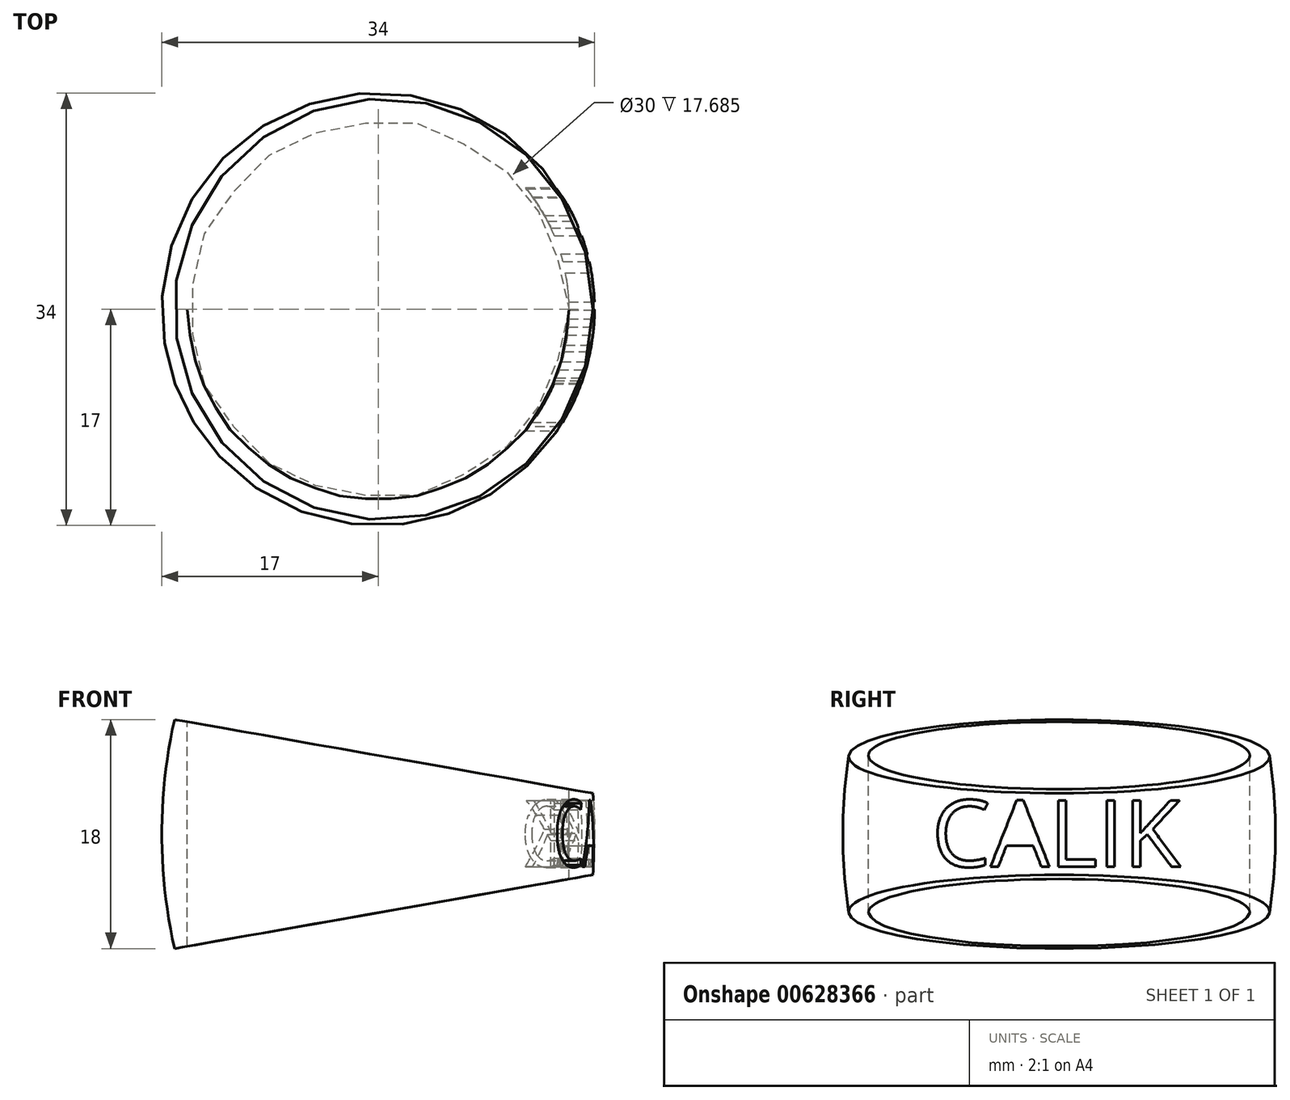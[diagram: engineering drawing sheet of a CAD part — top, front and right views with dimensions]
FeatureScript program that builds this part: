
annotation { "Feature Type Name" : "Feature", "Feature Type Description" : "" }
export const myFeature = defineFeature(function(context is Context, id is Id, definition is map)
    precondition{}
    {
        {
            var Q0;
            Q0=qCreatedBy(makeId("Front.planeOp"),FACE);
            var sketch = newSketch(context, id + "F0", { "sketchPlane" : qUnion([Q0])});
            skPoint(sketch, "E0", {"position": v(17, 0) * mm});
            skArc(sketch, "E1", {"start": v(16, -9) * mm, "mid": v(17, 0) * mm, "end": v(16, 9) * mm});
            skLineSegment(sketch, "E2", {"start": v(16, 9) * mm, "end": v(15, 9) * mm});
            skLineSegment(sketch, "E3", {"start": v(15, 9) * mm, "end": v(15, -9) * mm});
            skLineSegment(sketch, "E4", {"start": v(15, -9) * mm, "end": v(16, -9) * mm});
            skLineSegment(sketch, "E5", {"start": v(0, 0) * mm, "end": v(0, -4.95) * mm, "construction": true});
            skSolve(sketch);
        }
        {
            var Q0;
            Q0 = qSketchRegion(id + "F0", true);
            var Q1;
            Q1 = qConstructionFilter(qBodyType(qCreatedBy(id + "F0" ,EDGE), BodyType.WIRE), ConstructionObject.NO);
            var Q2;
            Q2=sQuery(id+"F0.wireOp",EDGE,"E5");
            revolve(context, id + "F1", {"entities" : qUnion([Q0]), "surfaceEntities" : qUnion([Q1]), "axis" : qUnion([Q2]), "revolveType" : RevolveType.FULL});
        }
        {
            var Q0;
            Q0=qCreatedBy(makeId("Front.planeOp"),FACE);
            cPlane(context, id + "F2", {"entities" : qUnion([Q0]), "cplaneType" : CPlaneType.OFFSET, "offset" : (17) * mm, "width" : 150 * mm, "height" : 150 * mm});
        }
        {
            var Q0;
            Q0=qCreatedBy(id+"F2.planeOp",FACE);
            var sketch = newSketch(context, id + "F3", { "sketchPlane" : qUnion([Q0])});
            skLineSegment(sketch, "E6", {"start": v(0, 0) * mm, "end": v(33.99, 0) * mm, "construction": true});
            skLineSegment(sketch, "E7.0", {"start": v(-16, 9) * mm, "end": v(16, 9) * mm});
            skLineSegment(sketch, "E8.0", {"start": v(-16, -9) * mm, "end": v(16, -9) * mm});
            skLineSegment(sketch, "E9", {"start": v(-16, 9) * mm, "end": v(18.47, 2.92) * mm});
            skLineSegment(sketch, "E10", {"start": v(18.47, 2.92) * mm, "end": v(16, 9) * mm});
            skLineSegment(sketch, "E11", {"start": v(-16, -9) * mm, "end": v(18.47, -2.92) * mm});
            skLineSegment(sketch, "E12", {"start": v(18.47, -2.92) * mm, "end": v(16, -9) * mm});
            skSolve(sketch);
        }
        {
            var Q0;
            Q0 = qSketchRegion(id + "F3", true);
            extrude(context, id + "F4", {"entities" : qUnion([Q0]), "operationType" : NewBodyOperationType.REMOVE, "oppositeDirection" : true, "depth" : 35 * mm, "offsetDistance" : 25 * mm});
        }
        {
            var Q0;
            Q0=qCreatedBy(makeId("Right.planeOp"),FACE);
            cPlane(context, id + "F5", {"entities" : qUnion([Q0]), "cplaneType" : CPlaneType.OFFSET, "offset" : (17) * mm, "width" : 150 * mm, "height" : 150 * mm});
        }
        {
            var Q0;
            Q0=qCreatedBy(id+"F5.planeOp",FACE);
            var sketch = newSketch(context, id + "F6", { "sketchPlane" : qUnion([Q0])});
            skText(sketch, "E13", { "text": "CALIK", "fontName": "OpenSans-Regular.ttf"});
            const initialGuessF6  = {"E13": [-0.01, -0.00256, 1, 0, 0.00526]};
            skSetInitialGuess(sketch, initialGuessF6);
            skSolve(sketch);
        }
        {
            var Q0;
            Q0 = qSketchRegion(id + "F6", true);
            var Q1;
            Q1=makeQuery(id+"F6.imprint","IMPRINT",FACE,{"disambiguationData":[TD([[makeQuery(id+"F6.imprint","IMPRINT",EDGE,{"derivedFrom":sQuery(id+"F6.wireOp",EDGE,"E13.sketch_text.stroke-23")}),1.0]])]});
            extrude(context, id + "F7", {"entities" : qUnion([Q0, Q1]), "operationType" : NewBodyOperationType.REMOVE, "oppositeDirection" : true, "depth" : 7 * mm, "offsetDistance" : 25 * mm});
        }
    });
